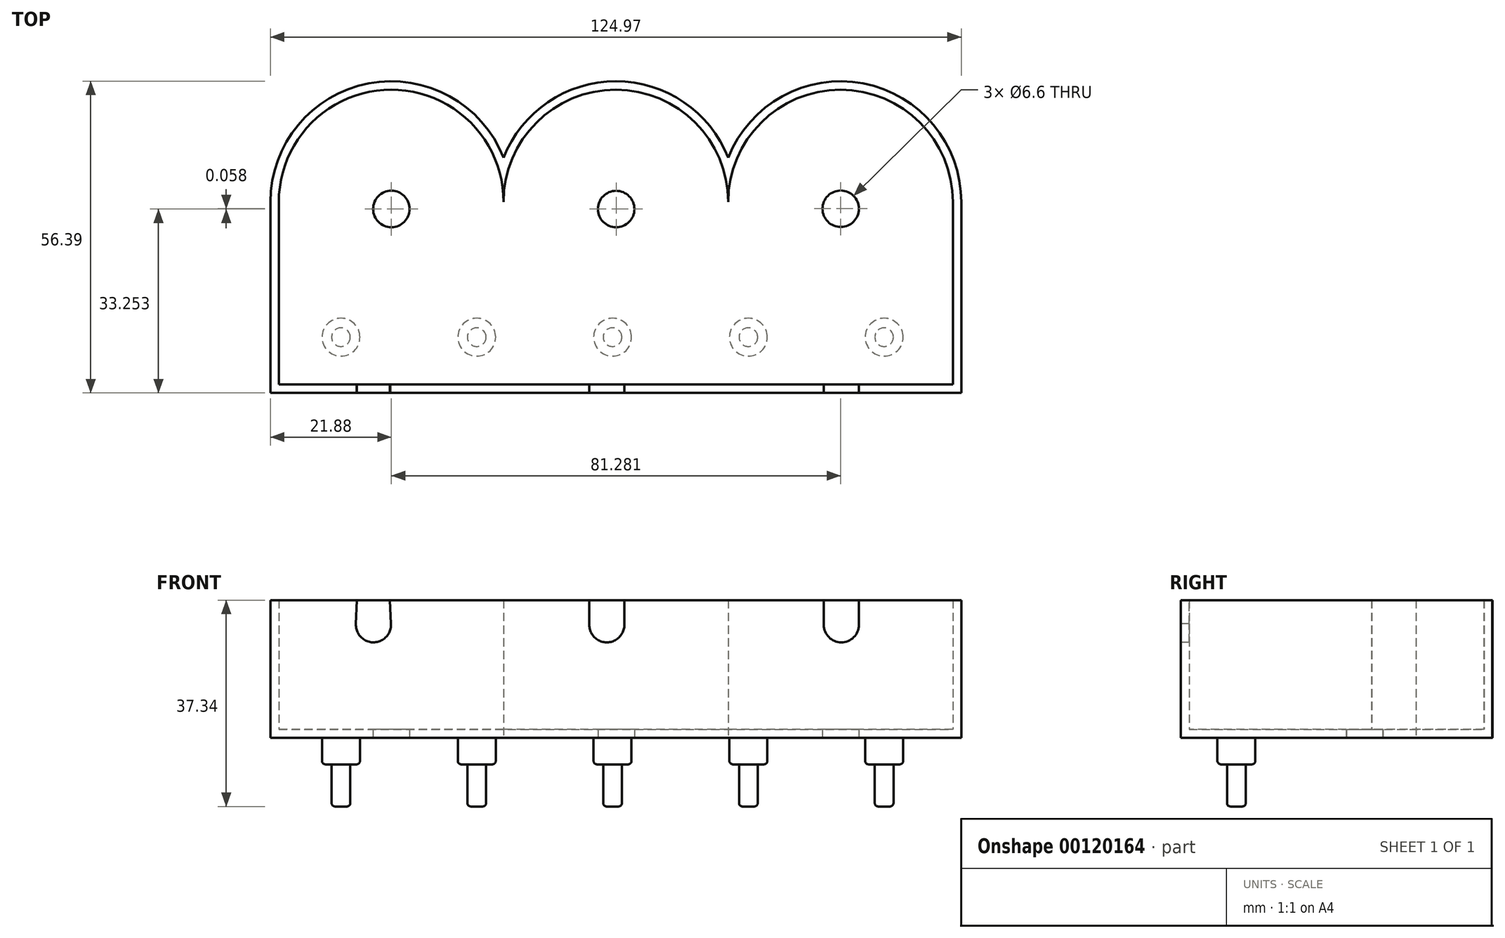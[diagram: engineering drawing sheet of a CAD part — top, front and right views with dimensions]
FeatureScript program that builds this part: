
annotation { "Feature Type Name" : "Feature", "Feature Type Description" : "" }
export const myFeature = defineFeature(function(context is Context, id is Id, definition is map)
    precondition{}
    {
        {
            var Q0;
            Q0=qCreatedBy(makeId("Top.planeOp"),FACE);
            var sketch = newSketch(context, id + "F0", { "sketchPlane" : qUnion([Q0])});
            skArc(sketch, "E0", {"start": v(-8.62, 13.3) * mm, "mid": v(-28.94, 33.61) * mm, "end": v(-49.26, 13.3) * mm, "construction": true});
            skCircle(sketch, "E1", {"center": v(-29.11, 12.03) * mm, "radius": 3.3 * mm, "construction": true});
            skLineSegment(sketch, "E2.top", {"start": v(-49.26, -19.73) * mm, "end": v(-8.62, -19.73) * mm, "construction": true});
            skLineSegment(sketch, "E2.left", {"start": v(-49.26, 13.3) * mm, "end": v(-49.26, -19.73) * mm, "construction": true});
            skLineSegment(sketch, "E3.trimOffspring", {"start": v(-8.62, 13.3) * mm, "end": v(-8.62, 13.3) * mm});
            skLineSegment(sketch, "E4", {"start": v(-8.62, -19.73) * mm, "end": v(32.02, -19.73) * mm, "construction": true});
            skLineSegment(sketch, "E5", {"start": v(32.02, 13.28) * mm, "end": v(32.02, 13.28) * mm});
            skArc(sketch, "E6", {"start": v(32.02, 13.28) * mm, "mid": v(11.7, 33.6) * mm, "end": v(-8.62, 13.3) * mm, "construction": true});
            skCircle(sketch, "E7", {"center": v(11.78, 12.02) * mm, "radius": 3.3 * mm, "construction": true});
            skLineSegment(sketch, "E8", {"start": v(32.02, -19.73) * mm, "end": v(72.66, -19.73) * mm, "construction": true});
            skLineSegment(sketch, "E9", {"start": v(72.66, -19.73) * mm, "end": v(72.66, 13.28) * mm, "construction": true});
            skArc(sketch, "E10", {"start": v(72.66, 13.28) * mm, "mid": v(52.34, 33.6) * mm, "end": v(32.02, 13.28) * mm, "construction": true});
            skCircle(sketch, "E11", {"center": v(52.34, 12.01) * mm, "radius": 3.3 * mm, "construction": true});
            skArc(sketch, "E12.0", {"start": v(74.18, 13.28) * mm, "mid": v(56.42, 34.74) * mm, "end": v(32.02, 21.3) * mm});
            skLineSegment(sketch, "E12.1", {"start": v(74.18, -21.25) * mm, "end": v(74.18, 13.28) * mm});
            skArc(sketch, "E12.2", {"start": v(32.02, 21.3) * mm, "mid": v(11.7, 35.13) * mm, "end": v(-8.62, 21.3) * mm});
            skLineSegment(sketch, "E12.3", {"start": v(32.02, -21.25) * mm, "end": v(74.18, -21.25) * mm});
            skArc(sketch, "E12.4", {"start": v(-8.62, 21.3) * mm, "mid": v(-33.02, 34.75) * mm, "end": v(-50.79, 13.3) * mm});
            skLineSegment(sketch, "E12.5", {"start": v(-50.79, 13.3) * mm, "end": v(-50.79, -21.25) * mm});
            skLineSegment(sketch, "E12.6", {"start": v(-50.79, -21.25) * mm, "end": v(-8.62, -21.25) * mm});
            skLineSegment(sketch, "E12.7", {"start": v(-8.62, -21.25) * mm, "end": v(32.02, -21.25) * mm});
            skSolve(sketch);
        }
        {
            var Q0;
            Q0=makeQuery(id+"F0.imprint","IMPRINT",FACE,{"disambiguationData":[TD([[makeQuery(id+"F0.imprint","IMPRINT",EDGE,{"derivedFrom":sQuery(id+"F0.wireOp",EDGE,"E12.0")}),1.0]])]});
            extrude(context, id + "F1", {"entities" : qUnion([Q0]), "depth" : 24.9 * mm});
        }
        {
            var Q0;
            Q0=makeQuery(id+"F1.opExtrude","CAP_FACE",FACE,{"disambiguationData":[OSD([sQuery(id+"F0.wireOp",EDGE,"E12.0"),sQuery(id+"F0.wireOp",EDGE,"E12.1"),sQuery(id+"F0.wireOp",EDGE,"E12.2"),sQuery(id+"F0.wireOp",EDGE,"E12.3"),sQuery(id+"F0.wireOp",EDGE,"E12.4"),sQuery(id+"F0.wireOp",EDGE,"E12.5"),sQuery(id+"F0.wireOp",EDGE,"E12.6"),sQuery(id+"F0.wireOp",EDGE,"E12.7")])],"isStart":false});
            shell(context, id + "F2", {"entities" : qUnion([Q0]), "thickness" : 1.52 * mm});
        }
        {
            var Q0;
            Q0=makeQuery(id+"F0.imprint","IMPRINT",FACE,{"disambiguationData":[TD([[makeQuery(id+"F0.imprint","IMPRINT",EDGE,{"derivedFrom":sQuery(id+"F0.wireOp",EDGE,"E12.0")}),1.0]])]});
            var sketch = newSketch(context, id + "F3", { "sketchPlane" : qUnion([Q0])});
            skPoint(sketch, "E13", {"position": v(-28.91, 13.34) * mm});
            skPoint(sketch, "E14", {"position": v(-28.91, 12.02) * mm});
            skCircle(sketch, "E15", {"center": v(-28.91, 12.02) * mm, "radius": 3.3 * mm});
            skPoint(sketch, "E16", {"position": v(11.75, 13.3) * mm});
            skPoint(sketch, "E17", {"position": v(11.75, 12) * mm});
            skCircle(sketch, "E18", {"center": v(11.75, 12) * mm, "radius": 3.3 * mm});
            skPoint(sketch, "E19", {"position": v(52.37, 12.06) * mm});
            skCircle(sketch, "E20", {"center": v(52.37, 12.06) * mm, "radius": 3.3 * mm});
            skSolve(sketch);
        }
        {
            var Q0;
            Q0 = qSketchRegion(id + "F3", true);
            extrude(context, id + "F4", {"entities" : qUnion([Q0]), "operationType" : NewBodyOperationType.REMOVE, "depth" : 25.4 * mm});
        }
        {
            var Q0;
            Q0=makeQuery(id+"F0.imprint","IMPRINT",FACE,{"disambiguationData":[TD([[makeQuery(id+"F0.imprint","IMPRINT",EDGE,{"derivedFrom":sQuery(id+"F0.wireOp",EDGE,"E12.0")}),1.0]])]});
            var sketch = newSketch(context, id + "F5", { "sketchPlane" : qUnion([Q0])});
            skPoint(sketch, "E21", {"position": v(11.08, 13.07) * mm});
            skPoint(sketch, "E22", {"position": v(-29.52, 13.36) * mm});
            skCircle(sketch, "E23", {"center": v(-38.02, -11.18) * mm, "radius": 3.43 * mm});
            skPoint(sketch, "E24", {"position": v(52.36, 13.28) * mm});
            skCircle(sketch, "E25.1.0.0", {"center": v(-13.46, -11.18) * mm, "radius": 3.43 * mm});
            skCircle(sketch, "E25.2.0.0", {"center": v(11.1, -11.18) * mm, "radius": 3.43 * mm});
            skCircle(sketch, "E25.3.0.0", {"center": v(35.66, -11.18) * mm, "radius": 3.43 * mm});
            skCircle(sketch, "E25.4.0.0", {"center": v(60.23, -11.18) * mm, "radius": 3.43 * mm});
            skLineSegment(sketch, "E25.direction1", {"start": v(-38.02, -11.18) * mm, "end": v(-13.46, -11.18) * mm, "construction": true});
            skSolve(sketch);
        }
        {
            var Q0;
            Q0 = qSketchRegion(id + "F5", true);
            extrude(context, id + "F6", {"entities" : qUnion([Q0]), "operationType" : NewBodyOperationType.ADD, "oppositeDirection" : true, "depth" : 4.83 * mm});
        }
        {
            var Q0;
            Q0=makeQuery(id+"F6.opExtrude","CAP_FACE",FACE,{"disambiguationData":[OSD([sQuery(id+"F5.wireOp",EDGE,"E23")])],"isStart":false});
            var sketch = newSketch(context, id + "F7", { "sketchPlane" : qUnion([Q0])});
            skCircle(sketch, "E26", {"center": v(-38.02, 11.18) * mm, "radius": 1.69 * mm});
            skCircle(sketch, "E27.1.0.0", {"center": v(-13.46, 11.18) * mm, "radius": 1.69 * mm});
            skCircle(sketch, "E27.2.0.0", {"center": v(11.1, 11.18) * mm, "radius": 1.69 * mm});
            skCircle(sketch, "E27.3.0.0", {"center": v(35.66, 11.18) * mm, "radius": 1.69 * mm});
            skCircle(sketch, "E27.4.0.0", {"center": v(60.22, 11.18) * mm, "radius": 1.69 * mm});
            skLineSegment(sketch, "E27.direction1", {"start": v(-38.02, 11.18) * mm, "end": v(-13.46, 11.18) * mm, "construction": true});
            skSolve(sketch);
        }
        {
            var Q0;
            Q0 = qSketchRegion(id + "F7", true);
            extrude(context, id + "F8", {"entities" : qUnion([Q0]), "operationType" : NewBodyOperationType.ADD, "depth" : 7.62 * mm});
        }
        {
            var Q0;
            Q0=makeQuery(id+"F8.opExtrude","CAP_FACE",FACE,{"disambiguationData":[OSD([sQuery(id+"F7.wireOp",EDGE,"E26")])],"isStart":false});
            var Q1;
            Q1=makeQuery(id+"F8.opExtrude","CAP_EDGE",EDGE,{"disambiguationData":[OSD([sQuery(id+"F7.wireOp",EDGE,"E27.1.0.0")])],"isStart":false});
            var Q2;
            Q2=makeQuery(id+"F8.opExtrude","CAP_EDGE",EDGE,{"disambiguationData":[OSD([sQuery(id+"F7.wireOp",EDGE,"E27.2.0.0")])],"isStart":false});
            var Q3;
            Q3=makeQuery(id+"F8.opExtrude","CAP_EDGE",EDGE,{"disambiguationData":[OSD([sQuery(id+"F7.wireOp",EDGE,"E27.3.0.0")])],"isStart":false});
            var Q4;
            Q4=makeQuery(id+"F8.opExtrude","CAP_EDGE",EDGE,{"disambiguationData":[OSD([sQuery(id+"F7.wireOp",EDGE,"E27.4.0.0")])],"isStart":false});
            var Q5;
            Q5=makeQuery(id+"F6.opExtrude","CAP_EDGE",EDGE,{"disambiguationData":[OSD([sQuery(id+"F5.wireOp",EDGE,"E25.4.0.0")])],"isStart":false});
            var Q6;
            Q6=makeQuery(id+"F6.opExtrude","CAP_EDGE",EDGE,{"disambiguationData":[OSD([sQuery(id+"F5.wireOp",EDGE,"E25.3.0.0")])],"isStart":false});
            var Q7;
            Q7=makeQuery(id+"F6.opExtrude","CAP_EDGE",EDGE,{"disambiguationData":[OSD([sQuery(id+"F5.wireOp",EDGE,"E25.2.0.0")])],"isStart":false});
            var Q8;
            Q8=makeQuery(id+"F6.opExtrude","CAP_EDGE",EDGE,{"disambiguationData":[OSD([sQuery(id+"F5.wireOp",EDGE,"E25.1.0.0")])],"isStart":false});
            var Q9;
            Q9=makeQuery(id+"F6.opExtrude","CAP_EDGE",EDGE,{"disambiguationData":[OSD([sQuery(id+"F5.wireOp",EDGE,"E23")])],"isStart":false});
            fillet(context, id + "F9", {"entities" : qUnion([Q0, Q1, Q2, Q3, Q4, Q5, Q6, Q7, Q8, Q9]), "radius" : 0.6 * mm, "tangentPropagation" : true, "allowEdgeOverflow" : false});
        }
        {
            var Q0;
            Q0=makeQuery(id+"F1.opExtrude","SWEPT_FACE",FACE,{"disambiguationData":[OSD([sQuery(id+"F0.wireOp",EDGE,"E12.3"),sQuery(id+"F0.wireOp",EDGE,"E12.6"),sQuery(id+"F0.wireOp",EDGE,"E12.7")])]});
            var sketch = newSketch(context, id + "F10", { "sketchPlane" : qUnion([Q0])});
            skCircle(sketch, "E28", {"center": v(-32.15, 20.42) * mm, "radius": 3.18 * mm});
            skLineSegment(sketch, "E29", {"start": v(-35.32, 20.52) * mm, "end": v(-35.18, 24.9) * mm});
            skLineSegment(sketch, "E30", {"start": v(-35.18, 24.9) * mm, "end": v(-29.2, 24.9) * mm});
            skLineSegment(sketch, "E31", {"start": v(-29.2, 24.9) * mm, "end": v(-28.98, 20.59) * mm});
            skCircle(sketch, "E32", {"center": v(10.06, 20.42) * mm, "radius": 3.18 * mm});
            skLineSegment(sketch, "E33", {"start": v(6.9, 20.22) * mm, "end": v(6.9, 24.9) * mm});
            skLineSegment(sketch, "E34", {"start": v(13.24, 20.42) * mm, "end": v(13.24, 24.9) * mm});
            skLineSegment(sketch, "E35", {"start": v(13.24, 24.9) * mm, "end": v(6.9, 24.9) * mm});
            skCircle(sketch, "E36", {"center": v(52.48, 20.42) * mm, "radius": 3.18 * mm});
            skLineSegment(sketch, "E37", {"start": v(55.66, 20.42) * mm, "end": v(55.66, 24.9) * mm});
            skLineSegment(sketch, "E38", {"start": v(49.3, 20.42) * mm, "end": v(49.3, 24.9) * mm});
            skLineSegment(sketch, "E39", {"start": v(55.66, 24.9) * mm, "end": v(49.3, 24.9) * mm});
            skSolve(sketch);
        }
        {
            var Q0;
            Q0 = qSketchRegion(id + "F10", true);
            extrude(context, id + "F11", {"entities" : qUnion([Q0]), "operationType" : NewBodyOperationType.REMOVE, "oppositeDirection" : true, "depth" : 12.7 * mm});
        }
    });
